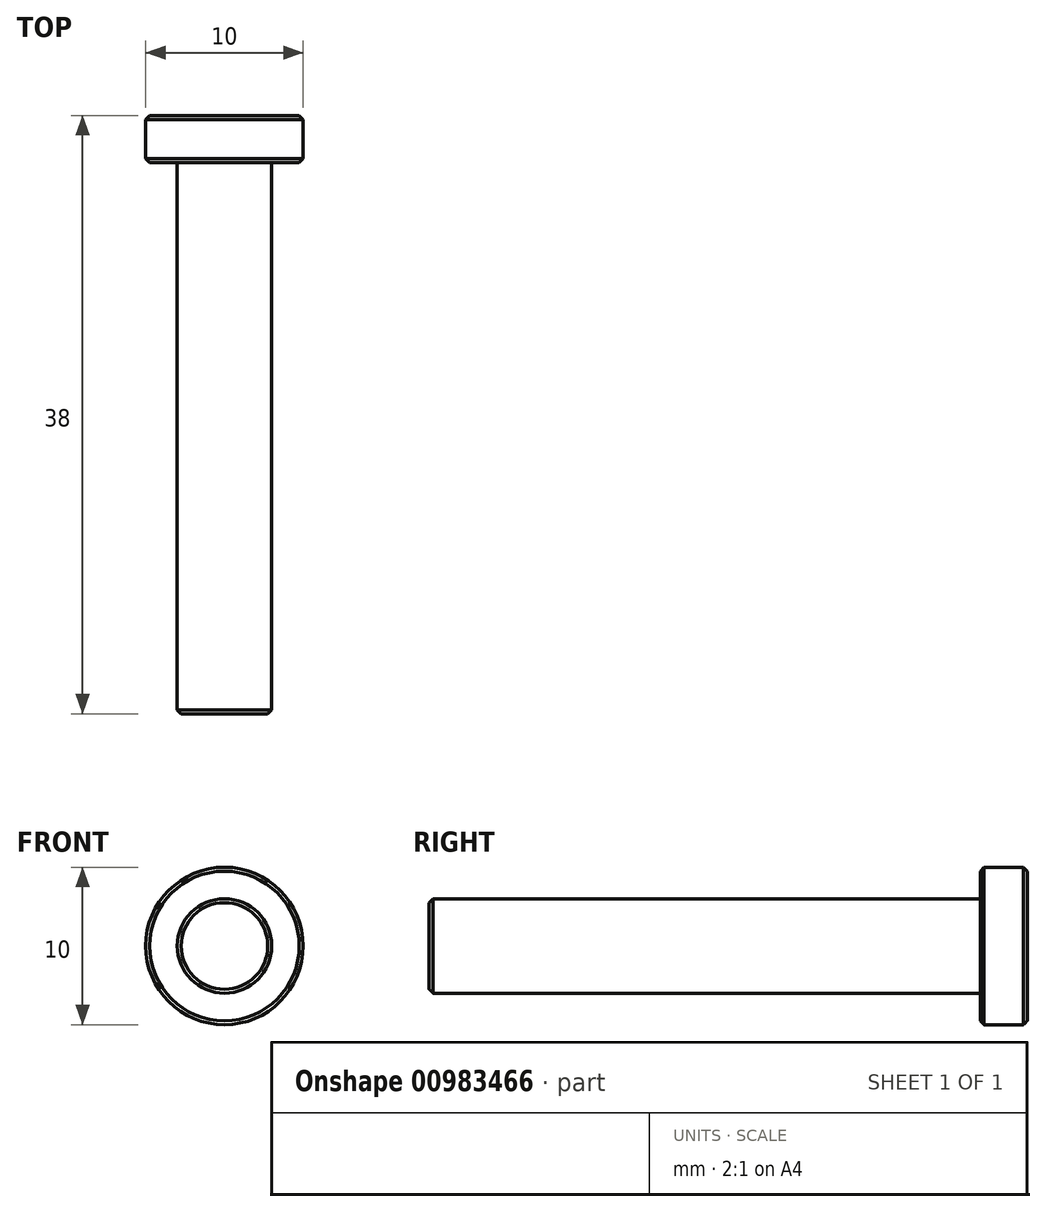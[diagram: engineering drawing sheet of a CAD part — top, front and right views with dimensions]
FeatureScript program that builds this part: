
annotation { "Feature Type Name" : "Feature", "Feature Type Description" : "" }
export const myFeature = defineFeature(function(context is Context, id is Id, definition is map)
    precondition{}
    {
        {
            var Q0;
            Q0=qCreatedBy(makeId("Front.planeOp"),FACE);
            var sketch = newSketch(context, id + "F0", { "sketchPlane" : qUnion([Q0])});
            skCircle(sketch, "E0", {"center": v(0, 0) * mm, "radius": 5 * mm});
            skSolve(sketch);
        }
        {
            var Q0;
            Q0 = qSketchRegion(id + "F0", true);
            extrude(context, id + "F1", {"entities" : qUnion([Q0]), "depth" : 3 * mm, "offsetDistance" : 25 * mm});
        }
        {
            var Q0;
            Q0=makeQuery(id+"F1.opExtrude","CAP_FACE",FACE,{"disambiguationData":[OSD([sQuery(id+"F0.wireOp",EDGE,"E0")])],"isStart":false});
            var sketch = newSketch(context, id + "F2", { "sketchPlane" : qUnion([Q0])});
            skCircle(sketch, "E1", {"center": v(0, 0) * mm, "radius": 3 * mm});
            skSolve(sketch);
        }
        {
            var Q0;
            Q0 = qSketchRegion(id + "F2", true);
            extrude(context, id + "F3", {"entities" : qUnion([Q0]), "operationType" : NewBodyOperationType.ADD, "depth" : 35 * mm, "offsetDistance" : 25 * mm});
        }
        {
            var Q0;
            Q0=makeQuery(id+"F1.opExtrude","CAP_EDGE",EDGE,{"disambiguationData":[OSD([sQuery(id+"F0.wireOp",EDGE,"E0")])],"isStart":true});
            var Q1;
            Q1=makeQuery(id+"F1.opExtrude","CAP_EDGE",EDGE,{"disambiguationData":[OSD([sQuery(id+"F0.wireOp",EDGE,"E0")])],"isStart":false});
            var Q2;
            Q2=makeQuery(id+"F3.opExtrude","CAP_EDGE",EDGE,{"disambiguationData":[OSD([sQuery(id+"F2.wireOp",EDGE,"E1")])],"isStart":false});
            chamfer(context, id + "F4", {"entities" : qUnion([Q0, Q1, Q2]), "width" : 0.25 * mm, "tangentPropagation" : true});
        }
    });
